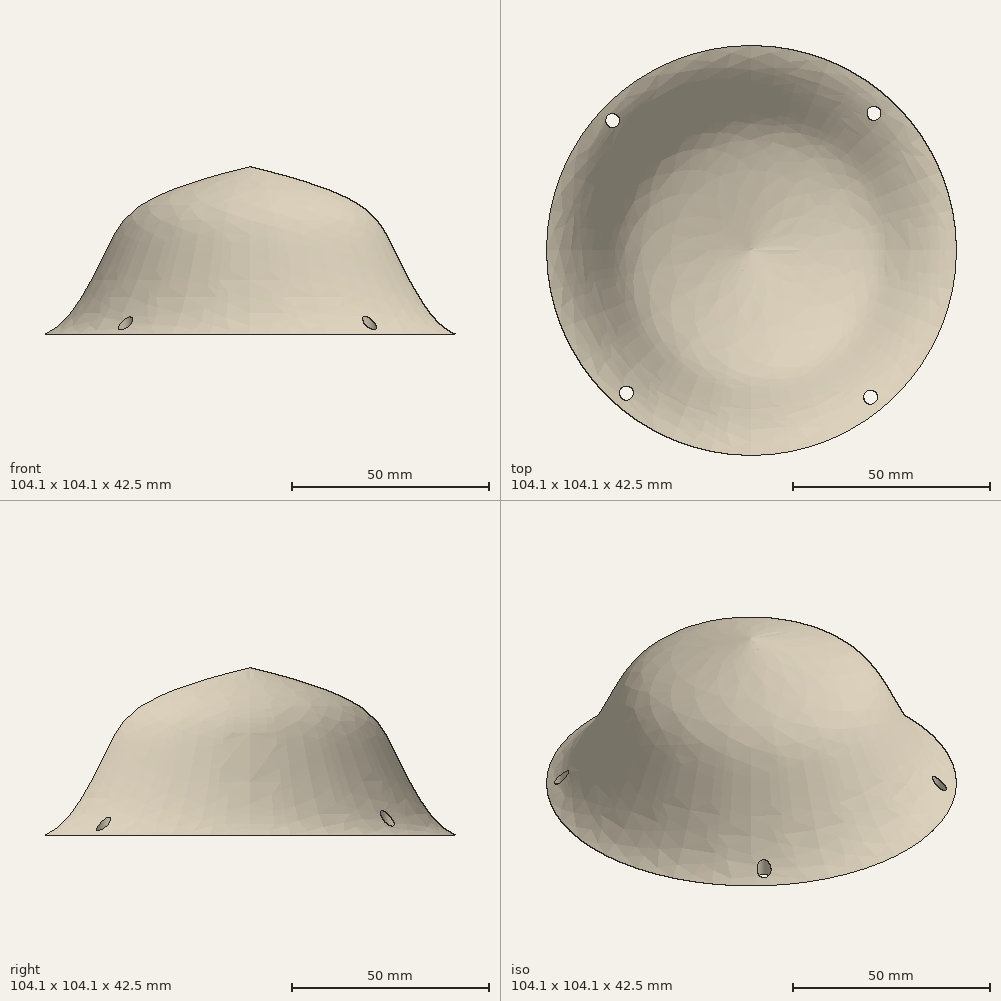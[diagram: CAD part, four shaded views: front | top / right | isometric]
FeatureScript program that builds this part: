
annotation { "Feature Type Name" : "Feature", "Feature Type Description" : "" }
export const myFeature = defineFeature(function(context is Context, id is Id, definition is map)
    precondition{}
    {
        {
            var Q0;
            Q0=qCreatedBy(makeId("Front.planeOp"),FACE);
            var sketch = newSketch(context, id + "F0", { "sketchPlane" : qUnion([Q0])});
            skLineSegment(sketch, "E0", {"start": v(0, -10.37) * mm, "end": v(0, 32.15) * mm});
            skLineSegment(sketch, "E1", {"start": v(0, -10.37) * mm, "end": v(69.16, -10.37) * mm});
            skFitSpline(sketch, "E2", {"points": [v(0, 32.15) * mm, v(28.24, 22.08) * mm, v(37.08, 9.96) * mm, v(52.07, -10.37) * mm, v(69.16, -10.37) * mm], "startDerivative": vector(110.8, -26.5) * mm, "endDerivative": vector(74.85, -21.79) * mm});
            skSolve(sketch);
        }
        {
            var Q0;
            {var subQ0=sQuery(id+"F0.wireOp",EDGE,"E0");Q0=makeQuery(id+"F0.imprint","IMPRINT",FACE,{"disambiguationData":[TD([[makeQuery(id+"F0.imprint","IMPRINT",EDGE,{"derivedFrom":subQ0}),-1.0]])]});}
            var Q1;
            Q1=sQuery(id+"F0.wireOp",EDGE,"E0");
            revolve(context, id + "F1", {"entities" : qUnion([Q0]), "axis" : qUnion([Q1]), "revolveType" : RevolveType.FULL});
        }
        {
            var Q0;
            Q0=qCreatedBy(makeId("Top.planeOp"),FACE);
            var sketch = newSketch(context, id + "F2", { "sketchPlane" : qUnion([Q0])});
            skCircle(sketch, "E3", {"center": v(-35.23, 32.97) * mm, "radius": 1.78 * mm});
            skCircle(sketch, "E4", {"center": v(31.12, 34.82) * mm, "radius": 1.78 * mm});
            skCircle(sketch, "E5", {"center": v(-31.74, -36.26) * mm, "radius": 1.78 * mm});
            skCircle(sketch, "E6", {"center": v(30.3, -37.28) * mm, "radius": 1.78 * mm});
            skSolve(sketch);
        }
        {
            var Q0;
            Q0=makeQuery(id+"F2.imprint","IMPRINT",FACE,{"disambiguationData":[TD([[makeQuery(id+"F2.imprint","IMPRINT",EDGE,{"derivedFrom":sQuery(id+"F2.wireOp",EDGE,"E5")}),1.0]])]});
            var Q1;
            Q1=makeQuery(id+"F2.imprint","IMPRINT",FACE,{"disambiguationData":[TD([[makeQuery(id+"F2.imprint","IMPRINT",EDGE,{"derivedFrom":sQuery(id+"F2.wireOp",EDGE,"E6")}),1.0]])]});
            var Q2;
            Q2=makeQuery(id+"F2.imprint","IMPRINT",FACE,{"disambiguationData":[TD([[makeQuery(id+"F2.imprint","IMPRINT",EDGE,{"derivedFrom":sQuery(id+"F2.wireOp",EDGE,"E4")}),1.0]])]});
            var Q3;
            Q3=makeQuery(id+"F2.imprint","IMPRINT",FACE,{"disambiguationData":[TD([[makeQuery(id+"F2.imprint","IMPRINT",EDGE,{"derivedFrom":sQuery(id+"F2.wireOp",EDGE,"E3")}),1.0]])]});
            extrude(context, id + "F3", {"entities" : qUnion([Q0, Q1, Q2, Q3]), "operationType" : NewBodyOperationType.REMOVE, "oppositeDirection" : true, "depth" : 25.4 * mm});
        }
    });
